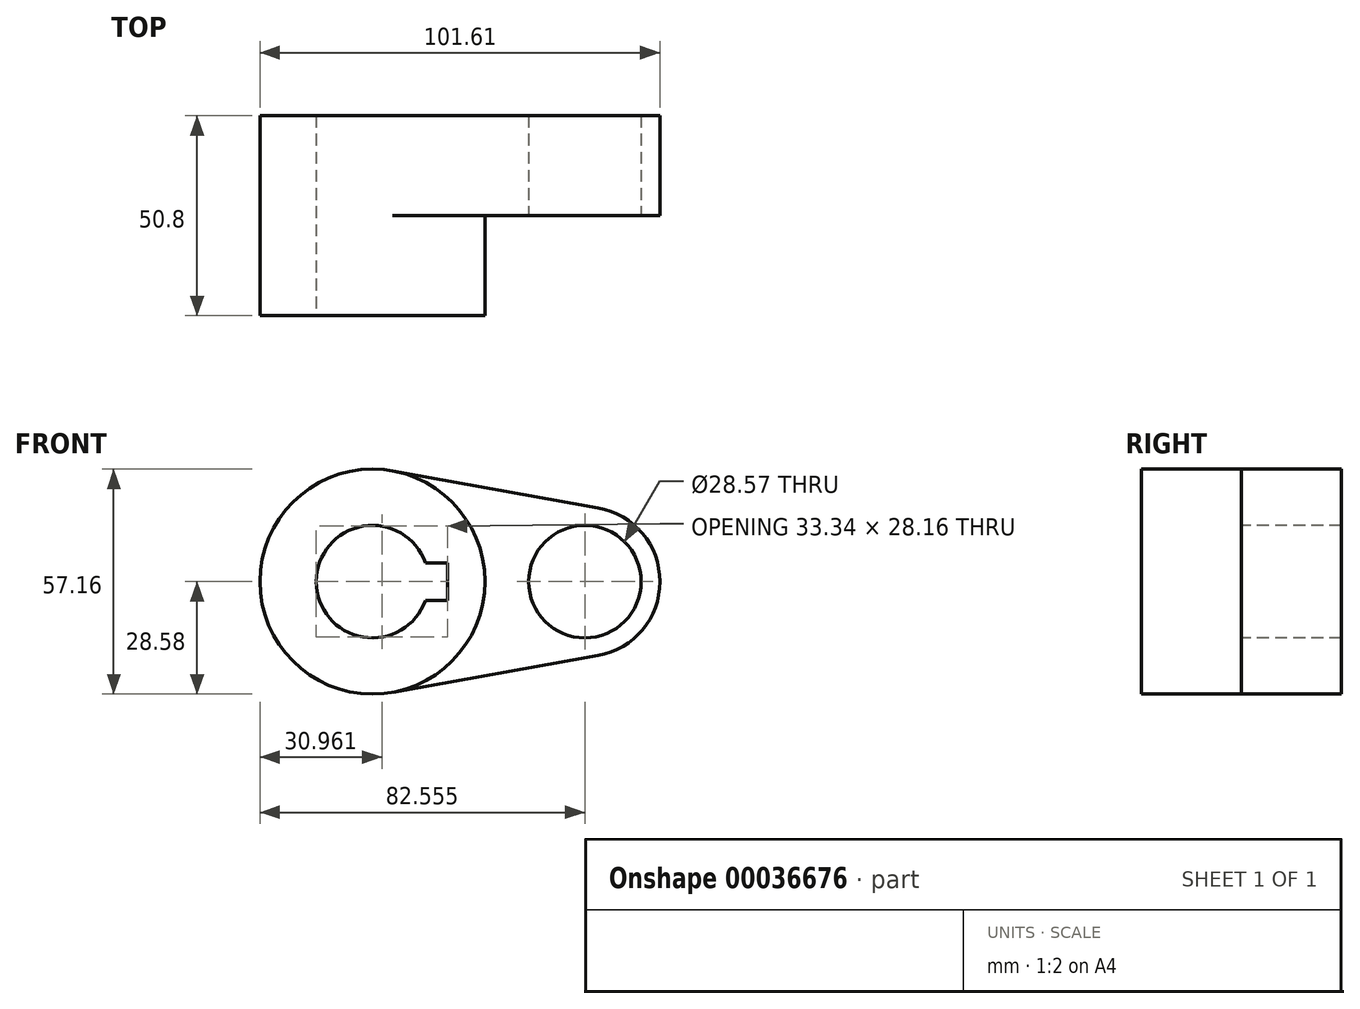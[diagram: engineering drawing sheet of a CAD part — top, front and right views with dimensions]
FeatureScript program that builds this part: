
annotation { "Feature Type Name" : "Feature", "Feature Type Description" : "" }
export const myFeature = defineFeature(function(context is Context, id is Id, definition is map)
    precondition{}
    {
        {
            var Q0;
            Q0=qCreatedBy(makeId("Front.planeOp"),FACE);
            var sketch = newSketch(context, id + "F0", { "sketchPlane" : qUnion([Q0])});
            skCircle(sketch, "E0", {"center": v(0, 0) * mm, "radius": 28.58 * mm});
            skCircle(sketch, "E1", {"center": v(53.98, 0) * mm, "radius": 19.05 * mm});
            skLineSegment(sketch, "E2", {"start": v(5.04, 28.13) * mm, "end": v(57.34, 18.75) * mm});
            skLineSegment(sketch, "E3", {"start": v(5.04, -28.13) * mm, "end": v(57.34, -18.75) * mm});
            skCircle(sketch, "E4", {"center": v(0, 0) * mm, "radius": 14.29 * mm});
            skCircle(sketch, "E5", {"center": v(53.98, 0) * mm, "radius": 14.29 * mm});
            skLineSegment(sketch, "E6.rect.bottom", {"start": v(-19.05, 4.76) * mm, "end": v(19.05, 4.76) * mm});
            skLineSegment(sketch, "E6.rect.top", {"start": v(-19.05, -4.76) * mm, "end": v(19.05, -4.76) * mm});
            skLineSegment(sketch, "E6.rect.left", {"start": v(-19.05, 4.76) * mm, "end": v(-19.05, -4.76) * mm});
            skLineSegment(sketch, "E6.rect.right", {"start": v(19.05, 4.76) * mm, "end": v(19.05, -4.76) * mm});
            skSolve(sketch);
        }
        {
            var Q0;
            {var subQ0=sQuery(id+"F0.wireOp",EDGE,"E6.rect.left");Q0=makeQuery(id+"F0.imprint","IMPRINT",FACE,{"disambiguationData":[TD([[makeQuery(id+"F0.imprint","IMPRINT",EDGE,{"derivedFrom":subQ0}),-1.0]])]});}
            var Q1;
            {var subQ0=sQuery(id+"F0.wireOp",EDGE,"E6.rect.left");Q1=makeQuery(id+"F0.imprint","IMPRINT",FACE,{"disambiguationData":[TD([[makeQuery(id+"F0.imprint","IMPRINT",EDGE,{"derivedFrom":subQ0}),1.0]])]});}
            var Q2;
            {var subQ1=sQuery(id+"F0.wireOp",EDGE,"E2");Q2=makeQuery(id+"F0.imprint","IMPRINT",FACE,{"disambiguationData":[TD([[makeQuery(id+"F0.imprint","IMPRINT",EDGE,{"derivedFrom":subQ1}),-1.0]])]});}
            var Q3;
            Q3=makeQuery(id+"F0.imprint","IMPRINT",FACE,{"disambiguationData":[TD([[makeQuery(id+"F0.imprint","IMPRINT",EDGE,{"derivedFrom":sQuery(id+"F0.wireOp",EDGE,"E5")}),-1.0]])]});
            extrude(context, id + "F1", {"entities" : qUnion([Q0, Q1, Q2, Q3]), "oppositeDirection" : true, "depth" : 25.4 * mm});
        }
        {
            var Q0;
            {var subQ0=sQuery(id+"F0.wireOp",EDGE,"E6.rect.left");Q0=makeQuery(id+"F0.imprint","IMPRINT",FACE,{"disambiguationData":[TD([[makeQuery(id+"F0.imprint","IMPRINT",EDGE,{"derivedFrom":subQ0}),-1.0]])]});}
            var Q1;
            {var subQ0=sQuery(id+"F0.wireOp",EDGE,"E6.rect.left");Q1=makeQuery(id+"F0.imprint","IMPRINT",FACE,{"disambiguationData":[TD([[makeQuery(id+"F0.imprint","IMPRINT",EDGE,{"derivedFrom":subQ0}),1.0]])]});}
            extrude(context, id + "F2", {"entities" : qUnion([Q0, Q1]), "operationType" : NewBodyOperationType.ADD, "depth" : 25.4 * mm});
        }
    });
